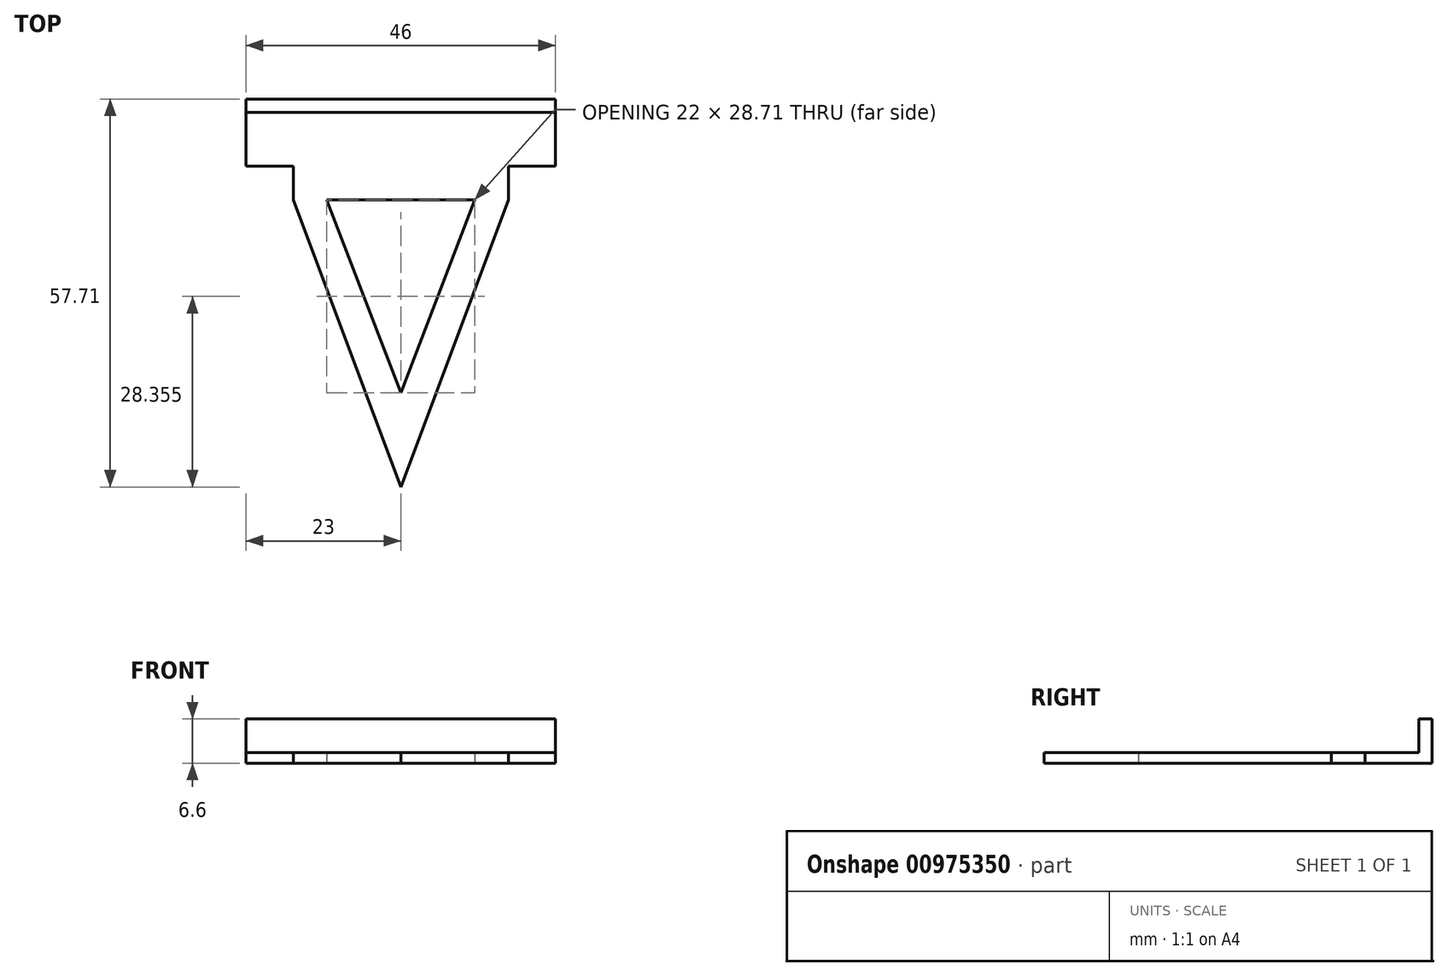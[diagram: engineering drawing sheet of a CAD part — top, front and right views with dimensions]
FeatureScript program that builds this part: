
annotation { "Feature Type Name" : "Feature", "Feature Type Description" : "" }
export const myFeature = defineFeature(function(context is Context, id is Id, definition is map)
    precondition{}
    {
        {
            var Q0;
            Q0=qCreatedBy(makeId("Top.planeOp"),FACE);
            var sketch = newSketch(context, id + "F0", { "sketchPlane" : qUnion([Q0])});
            skLineSegment(sketch, "E0", {"start": v(0, 0) * mm, "end": v(-23, 0) * mm});
            skLineSegment(sketch, "E1", {"start": v(-23, 0) * mm, "end": v(-23, -10) * mm});
            skLineSegment(sketch, "E2", {"start": v(-23, -10) * mm, "end": v(-16, -10) * mm});
            skLineSegment(sketch, "E3", {"start": v(-16, -10) * mm, "end": v(-16, -15) * mm});
            skLineSegment(sketch, "E4", {"start": v(-16, -15) * mm, "end": v(0, -57.71) * mm});
            skLineSegment(sketch, "E5", {"start": v(-11, -15) * mm, "end": v(0, -43.71) * mm});
            skLineSegment(sketch, "E6", {"start": v(-11, -15) * mm, "end": v(0, -15) * mm});
            skLineSegment(sketch, "E7.MirrorCS", {"start": v(11, -15) * mm, "end": v(0, -15) * mm});
            skLineSegment(sketch, "E8.MirrorCS", {"start": v(23, 0) * mm, "end": v(23, -10) * mm});
            skLineSegment(sketch, "E9.MirrorCS", {"start": v(16, -10) * mm, "end": v(16, -15) * mm});
            skLineSegment(sketch, "E10.MirrorCS", {"start": v(23, -10) * mm, "end": v(16, -10) * mm});
            skLineSegment(sketch, "E11.MirrorCS", {"start": v(16, -15) * mm, "end": v(0, -57.71) * mm});
            skLineSegment(sketch, "E12.MirrorCS", {"start": v(11, -15) * mm, "end": v(0, -43.71) * mm});
            skLineSegment(sketch, "E13.MirrorCS", {"start": v(0, 0) * mm, "end": v(23, 0) * mm});
            skSolve(sketch);
        }
        {
            var Q0;
            Q0 = qSketchRegion(id + "F0", true);
            extrude(context, id + "F1", {"entities" : qUnion([Q0]), "depth" : 1.6 * mm, "offsetDistance" : 25 * mm});
        }
        {
            var Q0;
            Q0=makeQuery(id+"F1.opExtrude","CAP_FACE",FACE,{"disambiguationData":[OSD([sQuery(id+"F0.wireOp",EDGE,"E0"),sQuery(id+"F0.wireOp",EDGE,"E1"),sQuery(id+"F0.wireOp",EDGE,"E2"),sQuery(id+"F0.wireOp",EDGE,"E3"),sQuery(id+"F0.wireOp",EDGE,"E4"),sQuery(id+"F0.wireOp",EDGE,"E5"),sQuery(id+"F0.wireOp",EDGE,"E6"),sQuery(id+"F0.wireOp",EDGE,"E7.MirrorCS"),sQuery(id+"F0.wireOp",EDGE,"E8.MirrorCS"),sQuery(id+"F0.wireOp",EDGE,"E9.MirrorCS"),sQuery(id+"F0.wireOp",EDGE,"E10.MirrorCS"),sQuery(id+"F0.wireOp",EDGE,"E11.MirrorCS"),sQuery(id+"F0.wireOp",EDGE,"E12.MirrorCS"),sQuery(id+"F0.wireOp",EDGE,"E13.MirrorCS")])],"isStart":false});
            var sketch = newSketch(context, id + "F2", { "sketchPlane" : qUnion([Q0])});
            skLineSegment(sketch, "E14.bottom", {"start": v(-23, 0) * mm, "end": v(23, 0) * mm});
            skLineSegment(sketch, "E14.top", {"start": v(-23, -2) * mm, "end": v(23, -2) * mm});
            skLineSegment(sketch, "E14.left", {"start": v(-23, 0) * mm, "end": v(-23, -2) * mm});
            skLineSegment(sketch, "E14.right", {"start": v(23, 0) * mm, "end": v(23, -2) * mm});
            skSolve(sketch);
        }
        {
            var Q0;
            Q0 = qSketchRegion(id + "F2", true);
            extrude(context, id + "F3", {"entities" : qUnion([Q0]), "operationType" : NewBodyOperationType.ADD, "depth" : 5 * mm, "offsetDistance" : 25 * mm});
        }
    });
